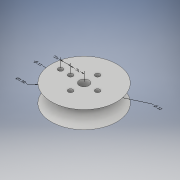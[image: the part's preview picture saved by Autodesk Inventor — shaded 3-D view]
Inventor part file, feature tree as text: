
AUTODESK INVENTOR PART (.ipt)
format: ipt  version: 2018 (Build 220112000, 112)  size: 173,568 bytes
history: native  units: in
note: dims shown in document units (in); Inventor stores cm internally (conversion verified against a paired STEP export)
features: other x7, sketch x4, extrude x3, chamfer x2
ambient origin geometry x8: Origin, YZ Plane, XZ Plane, XY Plane, X Axis, Y Axis, Z Axis, Center Point
bodies: Solid1 (feature_tree)
feature tree (16):
  other  "Annotations"
  extrude  "Extrusion1"  Depth=0.2in TaperAngle=0.0deg
  chamfer  "Chamfer1"  Distance=0.35in Angle=45.0deg
  extrude  "Extrusion2"  Depth=0.35in TaperAngle=45.0deg
  chamfer  "Chamfer2"  Distance=0.22in
  extrude  "Extrusion3"  Depth=0.11in
  sketch  "Sketch3"  dims[d15=0.31in]
  sketch  "Sketch1"  dims[d0=1.5in d1=0.2in d2=0.0in d7=0.35in d8=0.2in d9=45.0deg]
  sketch  "Sketch2"  dims[d10=0.2in d11=0.0in d12=0.35in d13=0.2in d14=45.0deg]
  sketch  "Sketch4"  dims[d16=0.23in d17=0.22in d18=0.11in d19=0.11in d20=0.31in d21=0.31in d22=0.31in d23=0.11in d24=0.11in d25=0.11in d28=0.22in d29=0.31in d30=0.23in d31=0.31in d32=0.31in d33=0.31in d34=0.11in d35=0.11in d36=0.11in d37=0.11in d38=0.11in d39=0.4in d40=0.0in d26=1.5792in d27=1.5in d41=0.3293in d42=1.5in d43=1.4463in d44=0.1321in d45=0.0594in d46=0.22in d47=0.0541in d48=0.0954in d49=0.31in d50=0.0598in d51=0.0586in d52=0.23in d53=-0.3764in d54=0.0667in d55=0.0375in d56=0.11in]
  other  "Diameter Dimension 1"
  other  "Diameter Dimension 2"
  other  "Diameter Dimension 3"
  other  "Linear Dimension 1"
  other  "Linear Dimension 2"
  other  "Diameter Dimension 4"
